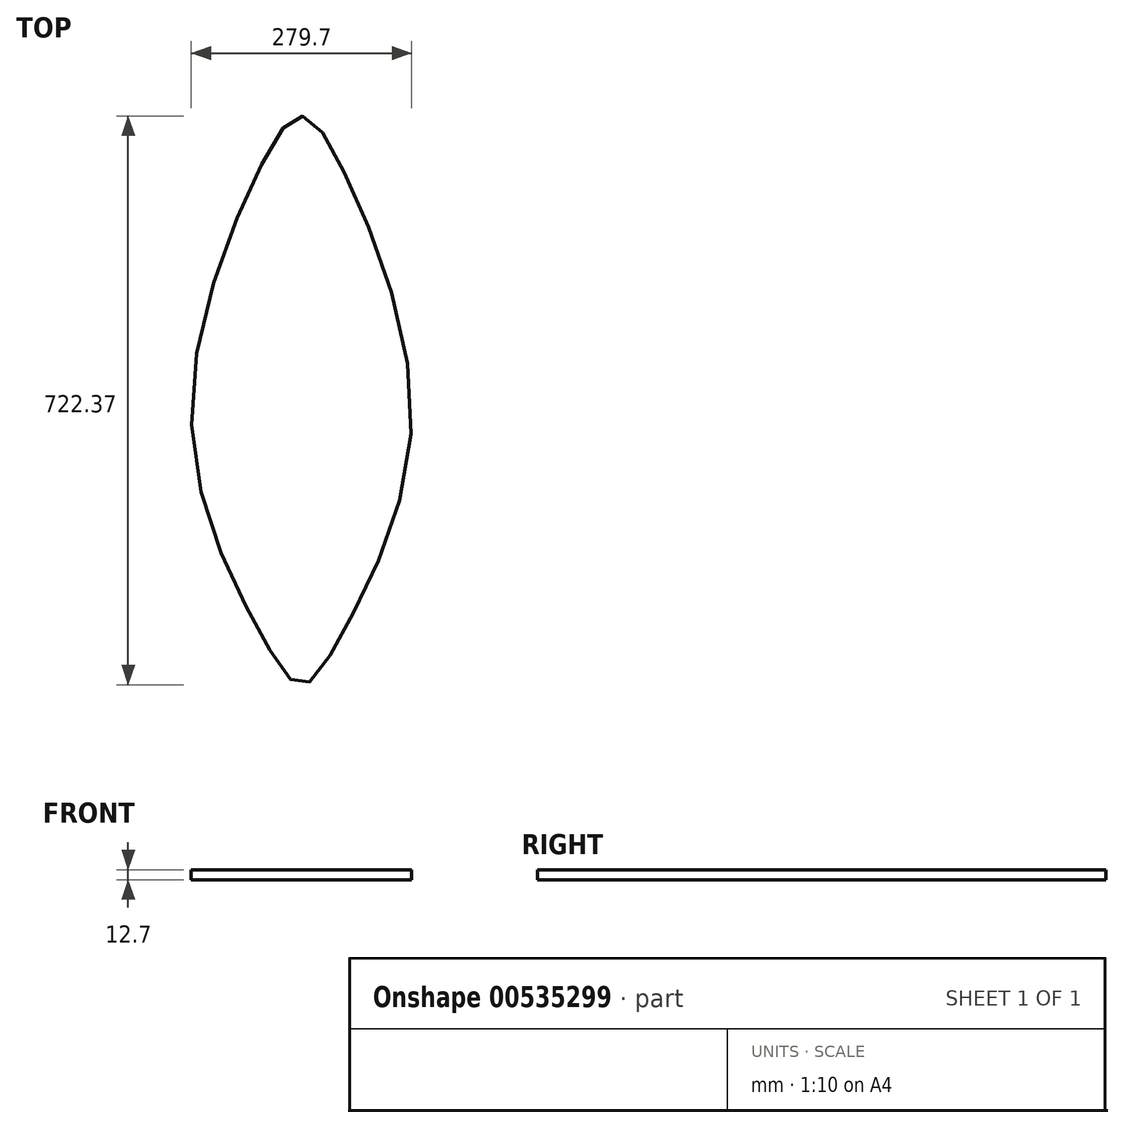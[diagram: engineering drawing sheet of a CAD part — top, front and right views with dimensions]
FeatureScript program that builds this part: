
annotation { "Feature Type Name" : "Feature", "Feature Type Description" : "" }
export const myFeature = defineFeature(function(context is Context, id is Id, definition is map)
    precondition{}
    {
        {
            var Q0;
            Q0=qCreatedBy(makeId("Top.planeOp"),FACE);
            var sketch = newSketch(context, id + "F0", { "sketchPlane" : qUnion([Q0])});
            skPoint(sketch, "E0.7.internal.snap0", {"position": v(0, -330.58) * mm});
            skFitSpline(sketch, "E0", {"points": [v(-50.76, 330.18) * mm, v(-139.7, 0) * mm, v(-50.8, -267.08) * mm, v(0, -330.58) * mm, v(50.8, -267.08) * mm, v(139.7, 0) * mm, v(50.8, 328.3) * mm, v(0, 391.8) * mm, v(-50.76, 330.18) * mm]});
            skSolve(sketch);
        }
        {
            var Q0;
            Q0=makeQuery(id+"F0.imprint","IMPRINT",FACE,{"disambiguationData":[TD([[makeQuery(id+"F0.imprint","IMPRINT",EDGE,{"derivedFrom":sQuery(id+"F0.wireOp",EDGE,"E0")}),1.0]])]});
            extrude(context, id + "F1", {"entities" : qUnion([Q0]), "depth" : 12.7 * mm, "offsetDistance" : 25.4 * mm});
        }
    });
